# Revit family: Mediterranean
name_source: partatom
category: Lighting Fixtures
units: mm (PartAtom-declared; Revit-internal decimal feet)

## family parameters
Cut with Voids When Loaded = No
Host = Face
Light Source = No
OmniClass Number = 23.80.70.14.21
OmniClass Title = Street and Roadway Lighting
Part Type = Normal
Room Calculation Point = No
Round Connector Dimension = Use Diameter
Shared = No

## types (12) — shared parameters
Apparent Load = 0 VA
Default Elevation = 48.00"
Description = Village Collection
Glass = Glass
Lamp = LED Array
Manufacturer = Beacon Products
Model = Mediterranean
Total Input Wattage = 55,80 & 110 Watts
URL = https://www.currentlighting.com
Voltage = 120 V

## per-type parameters (varying)
| type | Product Material |
| Basic Black Textured | Paint - Basic Black Textured |
| Black Matte Textured | Paint - Black Matte Textured |
| Bronze Textured | Paint - Bronze Textured |
| Dark Bronze Textured | Paint -Dark Bronze Textured |
| Dark Platinum Smooth | Paint - Dark Platinum Smooth |
| Gray Smooth | Paint -Gray Smooth |
| Green Textured | Paint - Green Textured |
| Metallic Bronze Textured | Paint - Metallic Bronze Textured |
| Metallic Silver Textured | Paint - Metallic Silver Textured |
| Metallic Titanium Textured | Paint -  Metallic Titanium Textured |
| Old World Iron | Paint - Old World Iron |
| White Texture | Paint -  White Texture |

## geometry (parser evidence)
native form markers: Sweep x5
no freeform markers — native parametric forms only
